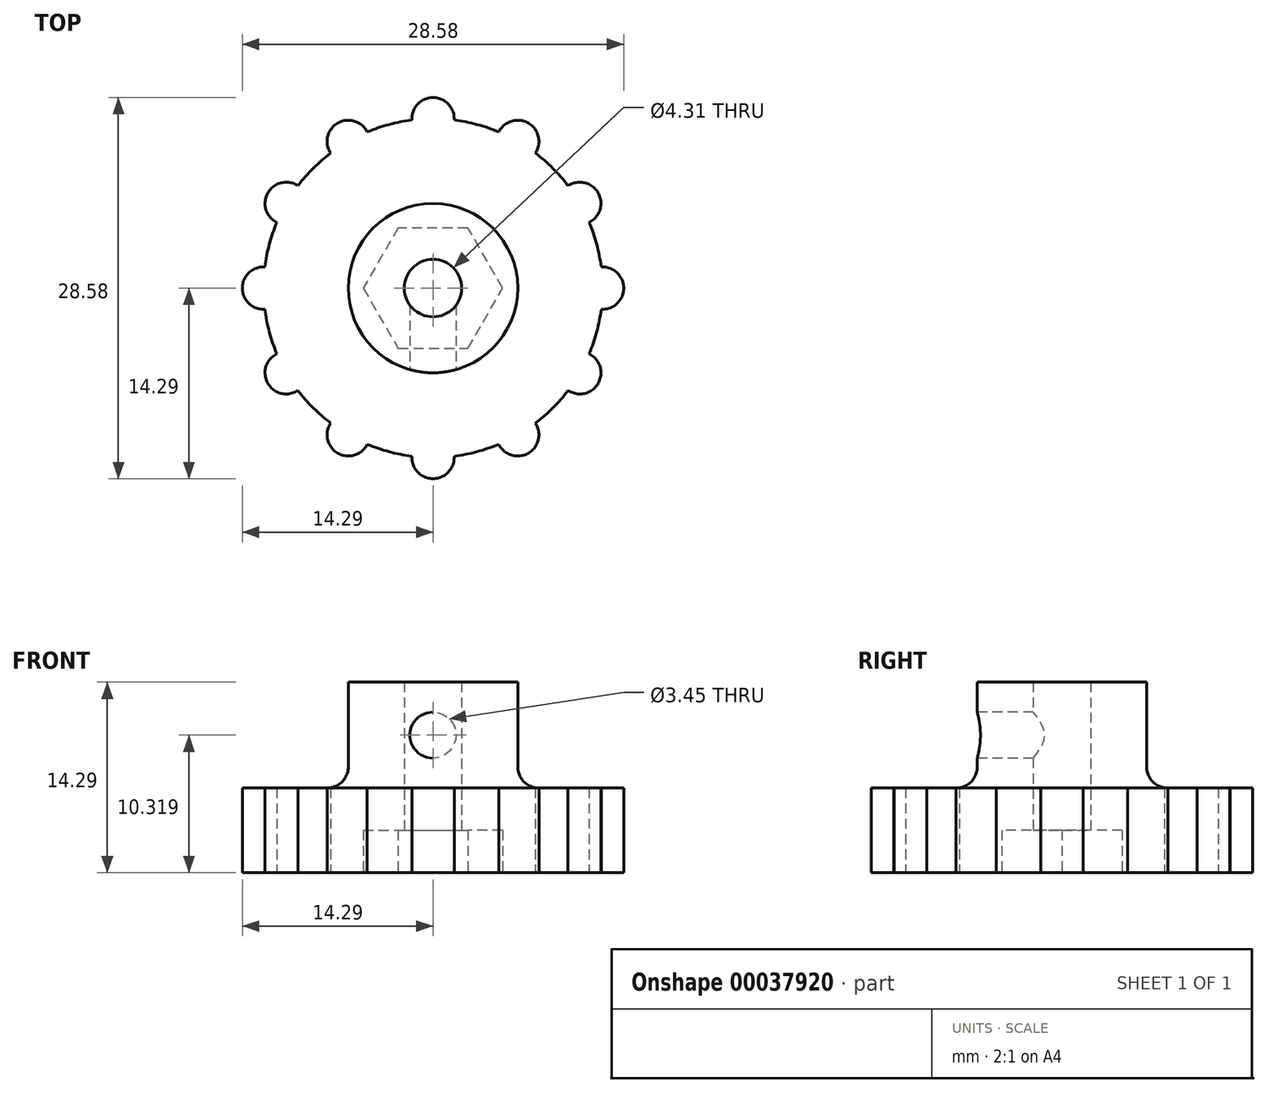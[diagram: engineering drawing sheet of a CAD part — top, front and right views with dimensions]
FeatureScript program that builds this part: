
annotation { "Feature Type Name" : "Feature", "Feature Type Description" : "" }
export const myFeature = defineFeature(function(context is Context, id is Id, definition is map)
    precondition{}
    {
        {
            var Q0;
            Q0=qCreatedBy(makeId("Top.planeOp"),FACE);
            var sketch = newSketch(context, id + "F0", { "sketchPlane" : qUnion([Q0])});
            skCircle(sketch, "E0", {"center": v(0, 0) * mm, "radius": 12.7 * mm});
            skSolve(sketch);
        }
        {
            var Q0;
            Q0=qSketchRegion(id+"F0",true);
            extrude(context, id + "F1", {"entities" : qUnion([Q0]), "depth" : 6.35 * mm});
        }
        {
            var Q0;
            Q0=makeQuery(id+"F1.opExtrude","CAP_FACE",FACE,{"disambiguationData":[OSD([sQuery(id+"F0.wireOp",EDGE,"E0")])],"isStart":true});
            var sketch = newSketch(context, id + "F2", { "sketchPlane" : qUnion([Q0])});
            skCircle(sketch, "E1.cCircle", {"center": v(0, 0) * mm, "radius": 4.52 * mm, "construction": true});
            skLineSegment(sketch, "E1.0", {"start": v(-2.61, 4.52) * mm, "end": v(2.61, 4.52) * mm});
            skLineSegment(sketch, "E1.1", {"start": v(2.61, 4.52) * mm, "end": v(5.22, 0) * mm});
            skLineSegment(sketch, "E1.2", {"start": v(5.22, 0) * mm, "end": v(2.61, -4.52) * mm});
            skLineSegment(sketch, "E1.3", {"start": v(2.61, -4.52) * mm, "end": v(-2.61, -4.52) * mm});
            skLineSegment(sketch, "E1.4", {"start": v(-2.61, -4.52) * mm, "end": v(-5.22, 0) * mm});
            skLineSegment(sketch, "E1.5", {"start": v(-5.22, 0) * mm, "end": v(-2.61, 4.52) * mm});
            skPoint(sketch, "E1.0.midPoint", {"position": v(0, 4.52) * mm});
            skSolve(sketch);
        }
        {
            var Q0;
            Q0=qSketchRegion(id+"F2",true);
            extrude(context, id + "F3", {"entities" : qUnion([Q0]), "operationType" : NewBodyOperationType.REMOVE, "oppositeDirection" : true, "depth" : 3.17 * mm});
        }
        {
            var Q0;
            Q0=makeQuery(id+"F1.opExtrude","CAP_FACE",FACE,{"disambiguationData":[OSD([sQuery(id+"F0.wireOp",EDGE,"E0")])],"isStart":false});
            var sketch = newSketch(context, id + "F4", { "sketchPlane" : qUnion([Q0])});
            skCircle(sketch, "E2", {"center": v(0, 0) * mm, "radius": 6.35 * mm, "construction": true});
            skLineSegment(sketch, "E3.rect.bottom", {"start": v(6.35, 6.35) * mm, "end": v(-6.35, 6.35) * mm});
            skLineSegment(sketch, "E3.rect.top", {"start": v(6.35, -6.35) * mm, "end": v(-6.35, -6.35) * mm});
            skLineSegment(sketch, "E3.rect.left", {"start": v(6.35, 6.35) * mm, "end": v(6.35, -6.35) * mm});
            skLineSegment(sketch, "E3.rect.right", {"start": v(-6.35, 6.35) * mm, "end": v(-6.35, -6.35) * mm});
            skSolve(sketch);
        }
        {
            var Q0;
            Q0=qSketchRegion(id+"F4",true);
            extrude(context, id + "F5", {"entities" : qUnion([Q0]), "operationType" : NewBodyOperationType.ADD, "depth" : 7.94 * mm});
        }
        {
            var Q0;
            Q0=makeQuery(id+"F1.opExtrude","CAP_FACE",FACE,{"disambiguationData":[OSD([sQuery(id+"F0.wireOp",EDGE,"E0")])],"isStart":true});
            var sketch = newSketch(context, id + "F6", { "sketchPlane" : qUnion([Q0])});
            skArc(sketch, "E4", {"start": v(1.58, 12.6) * mm, "mid": v(0, 14.29) * mm, "end": v(-1.58, 12.6) * mm});
            skArc(sketch, "E5", {"start": v(1.58, 12.6) * mm, "mid": v(0, 12.7) * mm, "end": v(-1.58, 12.6) * mm});
            skSolve(sketch);
        }
        {
            var Q0;
            Q0=qSketchRegion(id+"F6",true);
            var Q1;
            Q1=makeQuery(id+"F1.opExtrude","CAP_FACE",FACE,{"disambiguationData":[OSD([sQuery(id+"F0.wireOp",EDGE,"E0")])],"isStart":false});
            extrude(context, id + "F7", {"entities" : qUnion([Q0]), "operationType" : NewBodyOperationType.ADD, "endBound" : BoundingType.UP_TO_SURFACE, "oppositeDirection" : true, "endBoundEntityFace" : qUnion([Q1]), "depth" : 25.4 * mm});
        }
        {
            var Q0;
            Q0=makeQuery(id+"F7.opExtrude","SWEPT_FACE",FACE,{"disambiguationData":[OSD([sQuery(id+"F6.wireOp",EDGE,"E4")])]});
            var Q1;
            Q1=makeQuery(id+"F1.opExtrude","SWEPT_FACE",FACE,{"disambiguationData":[OSD([sQuery(id+"F0.wireOp",EDGE,"E0")])]});
            circularPattern(context, id + "F8", {"operationType" : NewBodyOperationType.ADD, "faces" : qUnion([Q0]), "axis" : qUnion([Q1]), "angle" : 30 * degree, "instanceCount" : round(12), "patternType" : PatternType.FACE});
        }
        {
            var Q0;
            Q0=makeQuery(id+"F3.boolean.opBoolean","COPY",FACE,{"derivedFrom":makeQuery(id+"F3.opExtrude","CAP_FACE",FACE,{"disambiguationData":[OSD([sQuery(id+"F2.wireOp",EDGE,"E1.0"),sQuery(id+"F2.wireOp",EDGE,"E1.1"),sQuery(id+"F2.wireOp",EDGE,"E1.2"),sQuery(id+"F2.wireOp",EDGE,"E1.3"),sQuery(id+"F2.wireOp",EDGE,"E1.4"),sQuery(id+"F2.wireOp",EDGE,"E1.5")])],"isStart":false})});
            var sketch = newSketch(context, id + "F9", { "sketchPlane" : qUnion([Q0])});
            skCircle(sketch, "E6", {"center": v(0, 0) * mm, "radius": 2.15 * mm});
            skSolve(sketch);
        }
        {
            var Q0;
            Q0 = qSketchRegion(id + "F9", true);
            var Q1;
            Q1=makeQuery(id+"F5.opExtrude","CAP_FACE",FACE,{"disambiguationData":[OSD([sQuery(id+"F4.wireOp",EDGE,"E3.rect.bottom"),sQuery(id+"F4.wireOp",EDGE,"E3.rect.top"),sQuery(id+"F4.wireOp",EDGE,"E3.rect.left"),sQuery(id+"F4.wireOp",EDGE,"E3.rect.right")])],"isStart":false});
            extrude(context, id + "F10", {"entities" : qUnion([Q0]), "operationType" : NewBodyOperationType.REMOVE, "endBound" : BoundingType.UP_TO_SURFACE, "oppositeDirection" : true, "endBoundEntityFace" : qUnion([Q1]), "depth" : 25.4 * mm});
        }
        {
            var Q0;
            Q0=makeQuery(id+"F5.opExtrude","SWEPT_FACE",FACE,{"disambiguationData":[OSD([sQuery(id+"F4.wireOp",EDGE,"E3.rect.top")])]});
            var sketch = newSketch(context, id + "F11", { "sketchPlane" : qUnion([Q0])});
            skLineSegment(sketch, "E7", {"start": v(0, 14.29) * mm, "end": v(0, 6.35) * mm, "construction": true});
            skCircle(sketch, "E8", {"center": v(0, 10.32) * mm, "radius": 1.73 * mm});
            skSolve(sketch);
        }
        {
            var Q0;
            Q0 = qSketchRegion(id + "F11", true);
            var Q1;
            Q1=makeQuery(id+"F10.boolean.opBoolean","COPY",FACE,{"derivedFrom":makeQuery(id+"F10.opExtrude","SWEPT_FACE",FACE,{"disambiguationData":[OSD([sQuery(id+"F9.wireOp",EDGE,"E6")])]})});
            extrude(context, id + "F12", {"entities" : qUnion([Q0]), "operationType" : NewBodyOperationType.REMOVE, "endBound" : BoundingType.UP_TO_SURFACE, "oppositeDirection" : true, "endBoundEntityFace" : qUnion([Q1]), "depth" : 25.4 * mm});
        }
        {
            var Q0;
            Q0=makeQuery(id+"F5.opExtrude","SWEPT_EDGE",EDGE,{"disambiguationData":[OSD([sQuery(id+"F4.wireOp",EDGE,"E3.rect.top"),sQuery(id+"F4.wireOp",EDGE,"E3.rect.right")])]});
            var Q1;
            Q1=makeQuery(id+"F5.opExtrude","SWEPT_EDGE",EDGE,{"disambiguationData":[OSD([sQuery(id+"F4.wireOp",EDGE,"E3.rect.top"),sQuery(id+"F4.wireOp",EDGE,"E3.rect.left")])]});
            var Q2;
            Q2=makeQuery(id+"F5.opExtrude","SWEPT_EDGE",EDGE,{"disambiguationData":[OSD([sQuery(id+"F4.wireOp",EDGE,"E3.rect.bottom"),sQuery(id+"F4.wireOp",EDGE,"E3.rect.left")])]});
            var Q3;
            Q3=makeQuery(id+"F5.opExtrude","SWEPT_EDGE",EDGE,{"disambiguationData":[OSD([sQuery(id+"F4.wireOp",EDGE,"E3.rect.bottom"),sQuery(id+"F4.wireOp",EDGE,"E3.rect.right")])]});
            fillet(context, id + "F13", {"entities" : qUnion([Q0, Q1, Q2, Q3]), "radius" : 6.35 * mm, "tangentPropagation" : true, "allowEdgeOverflow" : false});
        }
        {
            var Q0;
            Q0=makeQuery(id+"F13.opFillet","BLEND_EDGE",EDGE,{"blendedFrom":[makeQuery(id+"F5.opExtrude","SWEPT_EDGE",EDGE,{"disambiguationData":[OSD([sQuery(id+"F4.wireOp",EDGE,"E3.rect.bottom"),sQuery(id+"F4.wireOp",EDGE,"E3.rect.left")])]}),makeQuery(id+"F7.boolean.opBoolean","MERGE",FACE,{"derivedFrom":[makeQuery(id+"F1.opExtrude","CAP_FACE",FACE,{"disambiguationData":[OSD([sQuery(id+"F0.wireOp",EDGE,"E0")])],"isStart":false}),makeQuery(id+"F7.opExtrude","CAP_FACE",FACE,{"disambiguationData":[OSD([sQuery(id+"F6.wireOp",EDGE,"E4"),sQuery(id+"F6.wireOp",EDGE,"E5")])],"isStart":false})]})],"blendedInto":[makeQuery(id+"F7.boolean.opBoolean","MERGE",FACE,{"derivedFrom":[makeQuery(id+"F1.opExtrude","CAP_FACE",FACE,{"disambiguationData":[OSD([sQuery(id+"F0.wireOp",EDGE,"E0")])],"isStart":false}),makeQuery(id+"F7.opExtrude","CAP_FACE",FACE,{"disambiguationData":[OSD([sQuery(id+"F6.wireOp",EDGE,"E4"),sQuery(id+"F6.wireOp",EDGE,"E5")])],"isStart":false})]})]});
            fillet(context, id + "F14", {"entities" : qUnion([Q0]), "radius" : 1.59 * mm, "tangentPropagation" : true, "allowEdgeOverflow" : false});
        }
    });
